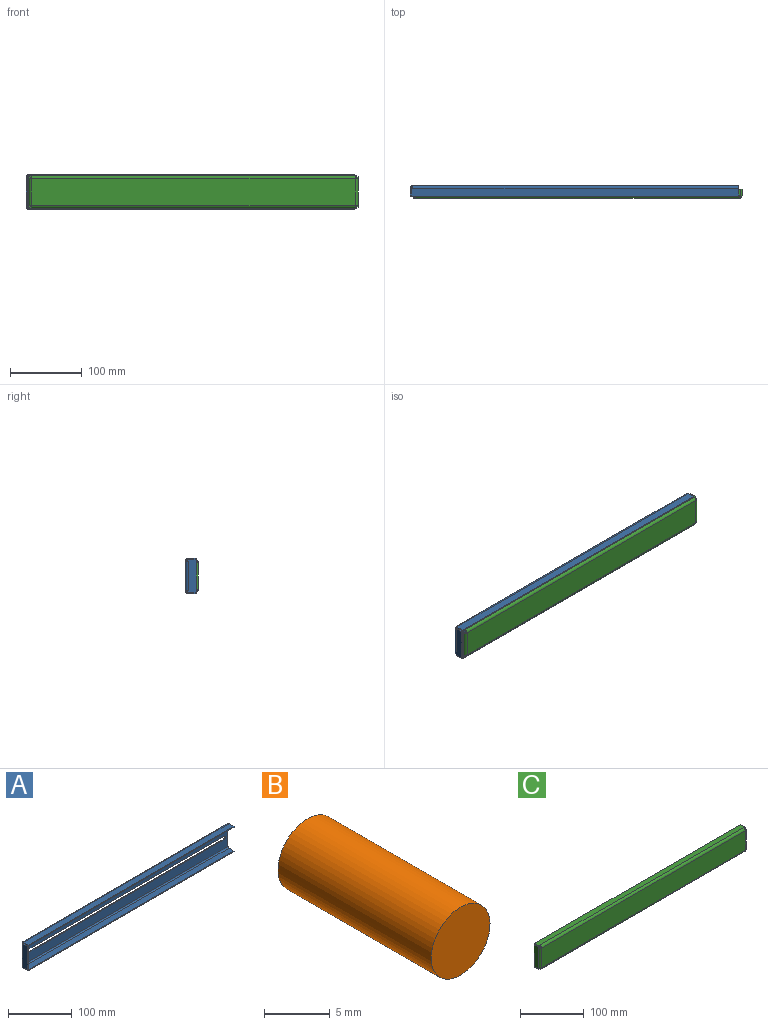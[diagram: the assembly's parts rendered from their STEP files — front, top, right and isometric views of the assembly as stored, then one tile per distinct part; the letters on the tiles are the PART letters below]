
ASSEMBLY  parts=3 mates=2
PART A: 38 faces, bbox 459.5x15x49 mm
  f0: plane 457.84x1.59mm, normal (0,-1,0), area 726.8mm2, adj f1,f3,f4,f5
  f1: plane 11.08x1.59mm, normal (1,0,0), area 17.6mm2, adj f0,f4,f5,f34
  f2: plane 2.26x1.59mm, normal (0,1,0), area 3.6mm2, adj f3,f4,f5,f35
  f3: plane 11.08x1.59mm, normal (-1,0,0), area 17.6mm2, adj f0,f2,f4,f5
  f4: plane 457.84x11.08mm, normal (0,0,1), area 5074.5mm2, adj f0,f1,f2,f3,f36
  f5: plane 457.84x11.08mm, normal (0,0,-1), area 5074.5mm2, adj f0,f1,f2,f3,f37
  f6: cylinder r=3.18mm len=6.35mm, axis (0,-1,0), area 15.8mm2, adj f7,f9,f11,f12
  f7: plane 438.15x1.59mm, normal (0,0,1), area 695.6mm2, adj f6,f8,f11,f12
  f8: cylinder r=3.18mm len=6.35mm, axis (0,-1,0), area 15.9mm2, adj f7,f9,f11,f12
  f9: plane 438.15x1.59mm, normal (0,0,-1), area 695.6mm2, adj f6,f8,f11,f12
  f10: plane 41.22x1.59mm, normal (1,0,0), area 65.4mm2, adj f11,f12,f19,f34
  f11: plane 455.58x41.22mm, normal (0,1,0), area 15963.9mm2, adj f6,f7,f8,f9,f10,f21,f32,f36
  f12: plane 455.58x41.22mm, normal (0,-1,0), area 15963.9mm2, adj f6,f7,f8,f9,f10,f22,f33,f37
  f13: plane 2.26x1.59mm, normal (0,1,0), area 3.6mm2, adj f15,f17,f18,f20
  f14: plane 457.84x1.59mm, normal (0,-1,0), area 726.8mm2, adj f15,f16,f17,f18
  f15: plane 11.08x1.59mm, normal (-1,0,0), area 17.6mm2, adj f13,f14,f17,f18
  f16: plane 11.08x1.59mm, normal (1,0,0), area 17.6mm2, adj f14,f17,f18,f19
  f17: plane 457.84x11.08mm, normal (0,0,-1), area 5074.5mm2, adj f13,f14,f15,f16,f21
  f18: plane 457.84x11.08mm, normal (0,0,1), area 5074.5mm2, adj f13,f14,f15,f16,f22
  f19: plane 3.87x3.87mm, normal (1,0,0), area 7.7mm2, adj f10,f16,f21,f22
  f20: plane 3.87x3.87mm, normal (-1,0,0), area 7.7mm2, adj f13,f21,f22,f30
  f21: cylinder r=3.87mm len=455.58mm, axis (1,0,0), area 2772mm2, adj f11,f17,f19,f20
  f22: cylinder r=2.29mm len=455.58mm, axis (1,0,0), area 1635.9mm2, adj f12,f18,f19,f20
  f23: plane 2.26x1.59mm, normal (0,1,0), area 3.6mm2, adj f25,f28,f29,f31
  f24: plane 45.74x1.59mm, normal (0,-1,0), area 72.6mm2, adj f25,f27,f28,f29
  f25: plane 11.08x1.59mm, normal (0,0,1), area 17.6mm2, adj f23,f24,f28,f29
  f26: plane 2.26x1.59mm, normal (0,1,0), area 3.6mm2, adj f27,f28,f29,f30
  f27: plane 11.08x1.59mm, normal (0,0,-1), area 17.6mm2, adj f24,f26,f28,f29
  f28: plane 45.74x11.08mm, normal (-1,0,0), area 506.9mm2, adj f23,f24,f25,f26,f27,f32
  f29: plane 45.74x11.08mm, normal (1,0,0), area 506.9mm2, adj f23,f24,f25,f26,f27,f33
  f30: plane 3.87x3.87mm, normal (0,0,-1), area 7.7mm2, adj f20,f26,f32,f33
  f31: plane 3.87x3.87mm, normal (0,0,1), area 7.7mm2, adj f23,f32,f33,f35
  f32: cylinder r=3.87mm len=41.22mm, axis (0,0,-1), area 250.8mm2, adj f11,f28,f30,f31
  f33: cylinder r=2.29mm len=41.22mm, axis (0,0,-1), area 148mm2, adj f12,f29,f30,f31
  f34: plane 3.87x3.87mm, normal (1,0,0), area 7.7mm2, adj f1,f10,f36,f37
  f35: plane 3.87x3.87mm, normal (-1,0,0), area 7.7mm2, adj f2,f31,f36,f37
  f36: cylinder r=3.87mm len=455.58mm, axis (1,0,0), area 2772mm2, adj f4,f11,f34,f35
  f37: cylinder r=2.29mm len=455.58mm, axis (1,0,0), area 1635.9mm2, adj f5,f12,f34,f35
PART B: 3 faces, bbox 6.4x16.5x6.4 mm
  f0: plane 6.35x6.35mm, normal (0,-1,0), area 31.7mm2, adj f1
  f1: cylinder r=3.17mm len=16.51mm, axis (0,1,0), area 329.4mm2, adj f0,f2
  f2: plane 6.35x6.35mm, normal (0,1,0), area 31.7mm2, adj f1
PART C: 46 faces, bbox 460.4x13x45.5 mm
  f0: plane 2.26x1.59mm, normal (0,-1,0), area 3.6mm2, adj f4,f5,f6,f43
  f1: plane 2.26x1.59mm, normal (0,-1,0), area 3.6mm2, adj f2,f5,f6,f42
  f2: plane 9.14x1.59mm, normal (1,0,0), area 14.5mm2, adj f1,f3,f5,f6
  f3: plane 457.15x1.59mm, normal (0,1,0), area 725.7mm2, adj f2,f4,f5,f6
  f4: plane 9.14x1.59mm, normal (-1,0,0), area 14.5mm2, adj f0,f3,f5,f6
  f5: plane 457.15x9.14mm, normal (0,0,1), area 4180.2mm2, adj f0,f1,f2,f3,f4,f44
  f6: plane 457.15x9.14mm, normal (0,0,-1), area 4180.2mm2, adj f0,f1,f2,f3,f4,f45
  f7: plane 452.63x37.73mm, normal (0,-1,0), area 17075.7mm2, adj f18,f29,f40,f44
  f8: plane 452.63x37.73mm, normal (0,1,0), area 17075.7mm2, adj f19,f30,f41,f45
  f9: plane 2.26x1.59mm, normal (0,-1,0), area 3.6mm2, adj f13,f14,f15,f16
  f10: plane 2.26x1.59mm, normal (0,-1,0), area 3.6mm2, adj f11,f14,f15,f17
  f11: plane 9.14x1.59mm, normal (-1,0,0), area 14.5mm2, adj f10,f12,f14,f15
  f12: plane 457.15x1.59mm, normal (0,1,0), area 725.7mm2, adj f11,f13,f14,f15
  f13: plane 9.14x1.59mm, normal (1,0,0), area 14.5mm2, adj f9,f12,f14,f15
  f14: plane 457.15x9.14mm, normal (0,0,-1), area 4180.2mm2, adj f9,f10,f11,f12,f13,f18
  f15: plane 457.15x9.14mm, normal (0,0,1), area 4180.2mm2, adj f9,f10,f11,f12,f13,f19
  f16: plane 3.87x3.87mm, normal (1,0,0), area 7.7mm2, adj f9,f18,f19,f38
  f17: plane 3.87x3.87mm, normal (-1,0,0), area 7.7mm2, adj f10,f18,f19,f27
  f18: cylinder r=3.87mm len=452.63mm, axis (1,0,0), area 2754mm2, adj f7,f14,f16,f17
  f19: cylinder r=2.29mm len=452.63mm, axis (1,0,0), area 1625.3mm2, adj f8,f15,f16,f17
  f20: plane 2.26x1.59mm, normal (0,-1,0), area 3.6mm2, adj f24,f25,f26,f27
  f21: plane 2.26x1.59mm, normal (0,-1,0), area 3.6mm2, adj f22,f25,f26,f28
  f22: plane 9.14x1.59mm, normal (0,0,1), area 14.5mm2, adj f21,f23,f25,f26
  f23: plane 42.25x1.59mm, normal (0,1,0), area 67.1mm2, adj f22,f24,f25,f26
  f24: plane 9.14x1.59mm, normal (0,0,-1), area 14.5mm2, adj f20,f23,f25,f26
  f25: plane 42.25x9.14mm, normal (-1,0,0), area 386.3mm2, adj f20,f21,f22,f23,f24,f29
  f26: plane 42.25x9.14mm, normal (1,0,0), area 386.3mm2, adj f20,f21,f22,f23,f24,f30
  f27: plane 3.87x3.87mm, normal (0,0,-1), area 7.7mm2, adj f17,f20,f29,f30
  f28: plane 3.87x3.87mm, normal (0,0,1), area 7.7mm2, adj f21,f29,f30,f43
  f29: cylinder r=3.87mm len=37.73mm, axis (0,0,-1), area 229.5mm2, adj f7,f25,f27,f28
  f30: cylinder r=2.29mm len=37.73mm, axis (0,0,-1), area 135.5mm2, adj f8,f26,f27,f28
  f31: plane 2.26x1.59mm, normal (0,-1,0), area 3.6mm2, adj f35,f36,f37,f39
  f32: plane 2.26x1.59mm, normal (0,-1,0), area 3.6mm2, adj f33,f36,f37,f38
  f33: plane 9.14x1.59mm, normal (0,0,-1), area 14.5mm2, adj f32,f34,f36,f37
  f34: plane 42.25x1.59mm, normal (0,1,0), area 67.1mm2, adj f33,f35,f36,f37
  f35: plane 9.14x1.59mm, normal (0,0,1), area 14.5mm2, adj f31,f34,f36,f37
  f36: plane 42.25x9.14mm, normal (1,0,0), area 386.3mm2, adj f31,f32,f33,f34,f35,f40
  f37: plane 42.25x9.14mm, normal (-1,0,0), area 386.3mm2, adj f31,f32,f33,f34,f35,f41
  f38: plane 3.87x3.87mm, normal (0,0,-1), area 7.7mm2, adj f16,f32,f40,f41
  f39: plane 3.87x3.87mm, normal (0,0,1), area 7.7mm2, adj f31,f40,f41,f42
  f40: cylinder r=3.87mm len=37.73mm, axis (0,0,-1), area 229.5mm2, adj f7,f36,f38,f39
  f41: cylinder r=2.29mm len=37.73mm, axis (0,0,-1), area 135.5mm2, adj f8,f37,f38,f39
  f42: plane 3.87x3.87mm, normal (1,0,0), area 7.7mm2, adj f1,f39,f44,f45
  f43: plane 3.87x3.87mm, normal (-1,0,0), area 7.7mm2, adj f0,f28,f44,f45
  f44: cylinder r=3.87mm len=452.63mm, axis (1,0,0), area 2754mm2, adj f5,f7,f42,f43
  f45: cylinder r=2.29mm len=452.63mm, axis (1,0,0), area 1625.3mm2, adj f6,f8,f42,f43
PLACE A rot(axis=(0,1,0),0deg) t=(-29.11,-37.13,44.68)mm
PLACE B rot(axis=(0,1,0),90deg) t=(-241.83,-39.96,254.23)mm
PLACE C rot(axis=(0,1,0),180deg) t=(-25.93,-39.96,44.68)mm
MATE fastened B.f1 <-> C.f8  axis (0,-1,0) through (-241.83,-51.39,44.68)mm
MATE pin_slot A.f8 <-> B.f1  axis (0,1,0) through (189.97,-34.88,44.68)mm
